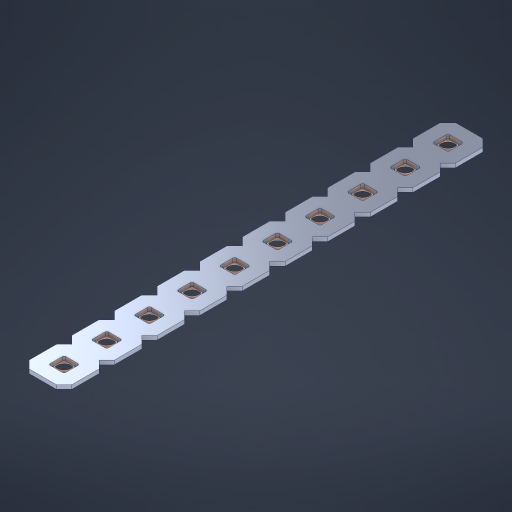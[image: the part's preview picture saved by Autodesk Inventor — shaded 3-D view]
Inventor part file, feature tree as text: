
AUTODESK INVENTOR PART (.ipt)
format: ipt  version: 2023 (Build 270158000, 158)  size: 388,608 bytes
history: native  units: in
note: dims shown in document units (in); Inventor stores cm internally (conversion verified against a paired STEP export)
features: other x11, extrude x9, sketch x2, pattern_linear x1
ambient origin geometry x8: Origin, YZ Plane, XZ Plane, XY Plane, X Axis, Y Axis, Z Axis, Center Point
bodies: Solid1 (feature_tree), Body (feature_tree)
feature tree (23):
  pattern_linear  "Rectangular Pattern1"  Spacing1=0.09in  [1 undecoded]
  sketch  "Sketch1"  dims[d1=0.5in]
  sketch  "Sketch2"  dims[d2=0.182in d3=0.09in d4=0.09in d5=0.09in d6=0.09in d7=0.09in d8=0.09in d9=0.09in d10=0.09in d11=0.02in d13=0.0in d14=0.172in d15=0.0625in d16=0.0in d19=0.5in d22=0.5in]
  other  "Srf1"
  other  "Srf126"
  other  "Srf127"
  other  "Srf128"
  other  "Srf129"
  other  "Srf130"
  other  "Srf131"
  other  "Srf250"
  other  "Srf251"
  other  "Srf252"
  other  "Circle"
  extrude  "ExtrusionSrf126"  Depth=0.09in
  extrude  "ExtrusionSrf127"  Depth=0.09in
  extrude  "ExtrusionSrf128"  Depth=0.09in
  extrude  "ExtrusionSrf129"  Depth=0.09in
  extrude  "ExtrusionSrf130"  Depth=0.09in
  extrude  "ExtrusionSrf131"  Depth=0.09in
  extrude  "ExtrusionSrf250"  Depth=0.09in
  extrude  "ExtrusionSrf251"  Depth=0.02in
  extrude  "ExtrusionSrf252"  TaperAngle=0.0deg  [1 undecoded]
note: 2 required parameter values undecoded (feature->parameter linkage not recoverable at this tier; creation-order binding heuristic only, values carry confidence <= 0.55)
